# Revit family: Gira_513300
name_source: partatom
category: Allgemeines Modell
revit_build: Autodesk Revit 2017 (Build: 20160225_1515(x64)
units: mm (PartAtom-declared; Revit-internal decimal feet)

## family parameters
Basisbauteil = Fläche
Beim Laden mit Abzugskörper schneiden = Nein
Bemaßung runder Anschluss = Durchmesser verwenden
Gemeinsam genutzt = Nein
Kann Basisbauteil für Bewehrung sein = Nein
Raumberechnungspunkt = Nein
Teiletyp = Normal

## types (1)
- Gira_513300
    BIM = https://media.stage.bim.site
    Beschreibung = KNX PB sens.3 Kmf 3g Sys55,KNX pushbutton sensor 3 Komfort, 3-gang,System 55, Gira E22,Start-up rocker,Features:,- Mounting on bus coupler 3.,- Disassembly safeguard by screw connection.,- Two multicoloured status LEDs per operating surface.,- Integrated temperature sensor for measuring and forwarding the ambient room temperature.,- Rocker or button function can be set for each operating surface.,- Rocker function: Switching, dimming, blind control, value transmitter 1-byte, value transmitter 2-byte, scene auxiliary unit, and room temperature controller auxiliary unit.,- Button function: Switching, dimming, blind control, value transmitter 1-byte, value transmitter 2-byte, scene auxiliary unit, and room temperature controller auxiliary unit.,- Controller auxiliary unit: Operating mode changeover with normal and high priority, defined selection of operating mode, toggle between various operating modes, switching of presence condition, setpoint offset.,- Blocker for blocking individual button or rocker functions.,- Alarm message displayed through all LEDs flashing.,- Multicoloured status LED (red, green, blue) can be configured globally or separately. A superimposed function can be activated on the bus whereby the colour and display information of individual status LEDs can be modified according to priority.,- Communication object for brightness control of status LED and illumination of inscription space (e.g. for reducing brightness in bedrooms at night).,- Inscription space illumination for rocker sets with inscription space.,- Illumination of inscription space ON, OFF, automatic switch-off, or switchable via object.,,Notes :,- Professional labelling with the Gira Inscription Service www.marking.gira.com.,- The pushbutton sensor is supplied with a program-neutral start-up rocker. The suitable rocker set for the design line must be ordered separately.
    Bus connection included = Nein
    Bus system KNX = Ja
    Bus system KNX radio = Nein
    Bus system LON = Nein
    Bus system Powernet = Nein
    Bus system radio frequent = Nein
    Colour = Other
    Data sheet = https://katalog.gira.de
    Degree of protection (IP) = IP20
    GTIN = 4010337086857
    HAN = 513300
    Hersteller = Gira
    Material = Other
    Material quality = Other
    Mounting method = Flush mounted (plaster)
    Number of actuation points = 6
    Number of buttons = 3
    Other bus systems = None
    Productwebsite = http://katalog.gira.de
    Surface finishing = Not applicable
    Surface protection = Other
    Transparent = Nein
    Typname = KNX PB sens.3 Komfort 3-g System 55, Gira E22
    URL = https://www.gira.de
    Vorgabe-Ansicht = 1219 mm
    With IR sensor = Nein
    With LED indication = Ja
    With anti-theft/dismantling protection = Ja
    With display = Nein
    With label area = Nein
    With room temperature controller = Ja

## geometry (parser evidence)
native form markers: Sweep x2
no freeform markers — native parametric forms only
